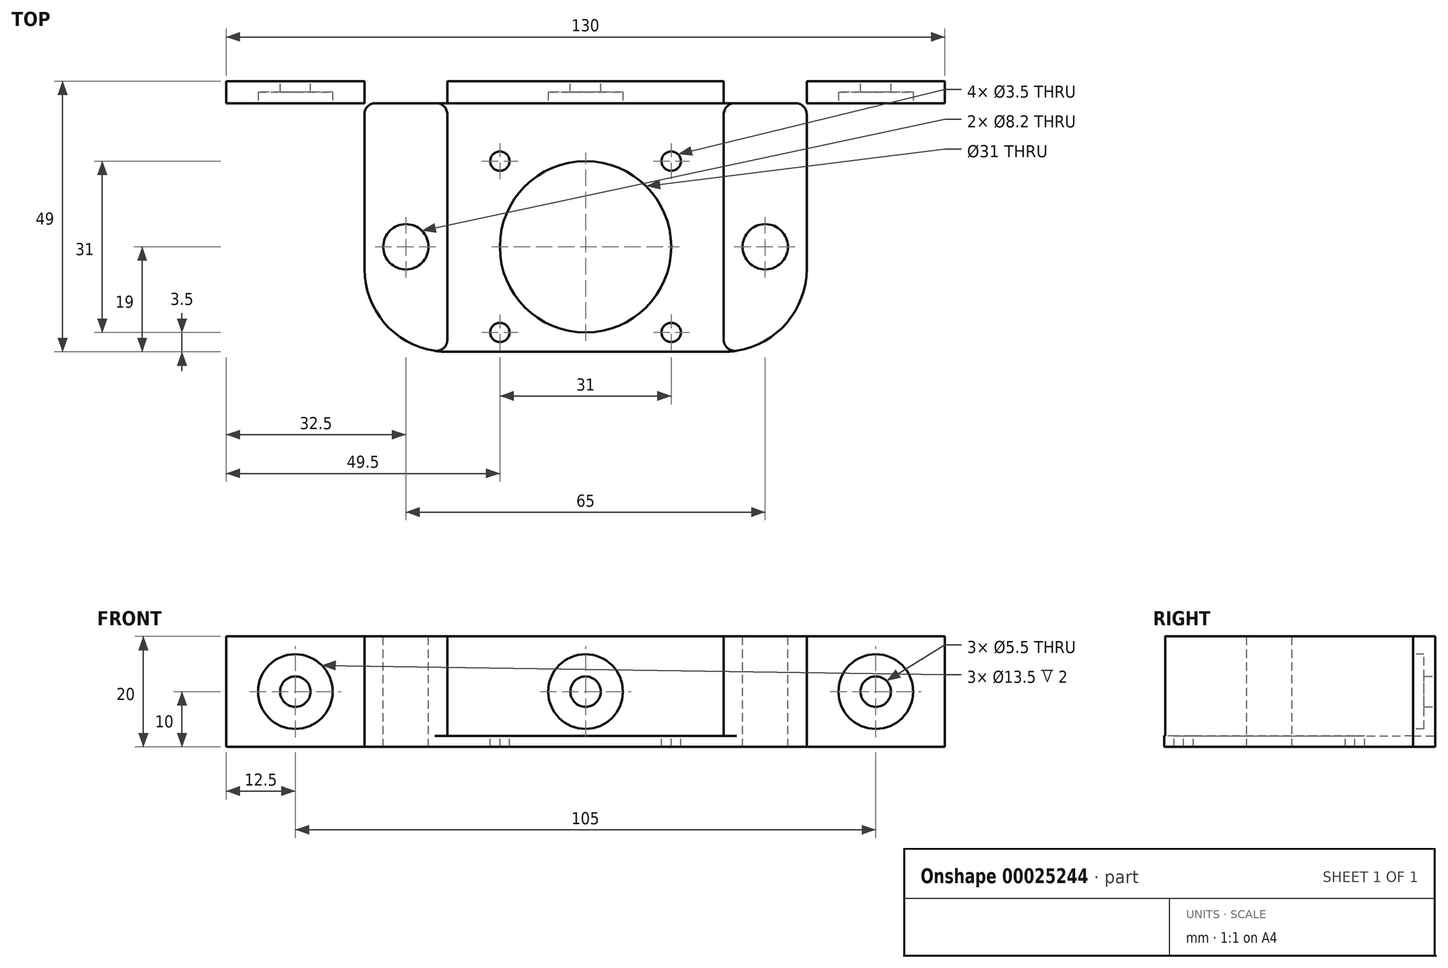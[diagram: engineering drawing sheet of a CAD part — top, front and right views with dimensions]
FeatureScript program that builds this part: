
annotation { "Feature Type Name" : "Feature", "Feature Type Description" : "" }
export const myFeature = defineFeature(function(context is Context, id is Id, definition is map)
    precondition{}
    {
        {
            var Q0;
            Q0=qCreatedBy(makeId("Front.planeOp"),FACE);
            var sketch = newSketch(context, id + "F0", { "sketchPlane" : qUnion([Q0])});
            skLineSegment(sketch, "E0.bottom", {"start": v(0, 0) * mm, "end": v(130, 0) * mm});
            skLineSegment(sketch, "E0.left", {"start": v(0, 0) * mm, "end": v(0, 20) * mm});
            skLineSegment(sketch, "E0.right", {"start": v(130, 0) * mm, "end": v(130, 20) * mm});
            skLineSegment(sketch, "E1.bottom", {"start": v(40, 20) * mm, "end": v(90, 20) * mm});
            skLineSegment(sketch, "E1.top", {"start": v(40, 0) * mm, "end": v(90, 0) * mm});
            skLineSegment(sketch, "E1.left", {"start": v(40, 20) * mm, "end": v(40, 0) * mm});
            skLineSegment(sketch, "E1.right", {"start": v(90, 20) * mm, "end": v(90, 0) * mm});
            skLineSegment(sketch, "E2", {"start": v(0, 20) * mm, "end": v(40, 20) * mm});
            skLineSegment(sketch, "E3", {"start": v(90, 20) * mm, "end": v(130, 20) * mm});
            skLineSegment(sketch, "E4.bottom", {"start": v(40, 20) * mm, "end": v(25, 20) * mm});
            skLineSegment(sketch, "E4.top", {"start": v(40, 0) * mm, "end": v(25, 0) * mm});
            skLineSegment(sketch, "E4.right", {"start": v(25, 20) * mm, "end": v(25, 0) * mm});
            skLineSegment(sketch, "E5.bottom", {"start": v(90, 20) * mm, "end": v(105, 20) * mm});
            skLineSegment(sketch, "E5.top", {"start": v(90, 0) * mm, "end": v(105, 0) * mm});
            skLineSegment(sketch, "E5.right", {"start": v(105, 20) * mm, "end": v(105, 0) * mm});
            skCircle(sketch, "E6", {"center": v(12.5, 10) * mm, "radius": 2.75 * mm});
            skCircle(sketch, "E7", {"center": v(117.5, 10) * mm, "radius": 2.75 * mm});
            skLineSegment(sketch, "E8.top", {"start": v(40, 2) * mm, "end": v(90, 2) * mm});
            skLineSegment(sketch, "E8.left", {"start": v(40, 0) * mm, "end": v(40, 2) * mm});
            skLineSegment(sketch, "E8.right", {"start": v(90, 0) * mm, "end": v(90, 2) * mm});
            skLineSegment(sketch, "E9", {"start": v(0, 10) * mm, "end": v(12.5, 10) * mm});
            skLineSegment(sketch, "E10", {"start": v(12.5, 10) * mm, "end": v(65, 10) * mm});
            skLineSegment(sketch, "E11", {"start": v(117.5, 10) * mm, "end": v(65, 10) * mm});
            skLineSegment(sketch, "E12", {"start": v(117.5, 10) * mm, "end": v(130, 10) * mm});
            skCircle(sketch, "E13", {"center": v(12.5, 10) * mm, "radius": 6.75 * mm});
            skCircle(sketch, "E14", {"center": v(117.5, 10) * mm, "radius": 6.75 * mm});
            skCircle(sketch, "E15", {"center": v(65, 10) * mm, "radius": 2.75 * mm});
            skCircle(sketch, "E16", {"center": v(65.03, 10.1) * mm, "radius": 6.75 * mm});
            skSolve(sketch);
        }
        {
            var Q0;
            {var subQ1=sQuery(id+"F0.wireOp",EDGE,"E0.left");Q0=makeQuery(id+"F0.imprint","IMPRINT",FACE,{"disambiguationData":[TD([[makeQuery(id+"F0.imprint","IMPRINT",EDGE,{"derivedFrom":subQ1}),-1.0]])]});}
            var Q1;
            {var subQ1=sQuery(id+"F0.wireOp",EDGE,"E0.right");Q1=makeQuery(id+"F0.imprint","IMPRINT",FACE,{"disambiguationData":[TD([[makeQuery(id+"F0.imprint","IMPRINT",EDGE,{"derivedFrom":subQ1}),1.0]])]});}
            var Q2;
            Q2=makeQuery(id+"F0.imprint","IMPRINT",FACE,{"disambiguationData":[TD([[makeQuery(id+"F0.imprint","IMPRINT",EDGE,{"derivedFrom":sQuery(id+"F0.wireOp",EDGE,"E1.bottom")}),-1.0]])]});
            var Q3;
            Q3=makeQuery(id+"F0.imprint","IMPRINT",FACE,{"disambiguationData":[TD([[makeQuery(id+"F0.imprint","IMPRINT",EDGE,{"derivedFrom":sQuery(id+"F0.wireOp",EDGE,"E4.bottom")}),1.0]])]});
            var Q4;
            Q4=makeQuery(id+"F0.imprint","IMPRINT",FACE,{"disambiguationData":[TD([[makeQuery(id+"F0.imprint","IMPRINT",EDGE,{"derivedFrom":sQuery(id+"F0.wireOp",EDGE,"E5.bottom")}),-1.0]])]});
            var Q5;
            Q5=makeQuery(id+"F0.imprint","IMPRINT",FACE,{"disambiguationData":[TD([[makeQuery(id+"F0.imprint","IMPRINT",EDGE,{"derivedFrom":sQuery(id+"F0.wireOp",EDGE,"E1.top")}),1.0]])]});
            var Q6;
            {var subQ6=sQuery(id+"F0.wireOp",EDGE,"E4.top");Q6=makeQuery(id+"F0.imprint","IMPRINT",FACE,{"disambiguationData":[TD([[makeQuery(id+"F0.imprint","IMPRINT",EDGE,{"derivedFrom":subQ6}),-1.0]])]});}
            var Q7;
            {var subQ9=sQuery(id+"F0.wireOp",EDGE,"E8.top");Q7=makeQuery(id+"F0.imprint","IMPRINT",FACE,{"disambiguationData":[TD([[makeQuery(id+"F0.imprint","IMPRINT",EDGE,{"derivedFrom":subQ9}),1.0]])]});}
            var Q8;
            {var subQ6=sQuery(id+"F0.wireOp",EDGE,"E5.top");Q8=makeQuery(id+"F0.imprint","IMPRINT",FACE,{"disambiguationData":[TD([[makeQuery(id+"F0.imprint","IMPRINT",EDGE,{"derivedFrom":subQ6}),1.0]])]});}
            var Q9;
            {var subQ3=sQuery(id+"F0.wireOp",EDGE,"E9");var subQ5=sQuery(id+"F0.wireOp",EDGE,"E6");var subQ7=makeQuery(id+"F0.imprint","INTERSECT",VERTEX,{"derivedFrom":[subQ5,subQ3]});Q9=makeQuery(id+"F0.imprint","IMPRINT",FACE,{"disambiguationData":[TD([[makeQuery(id+"F0.imprint","IMPRINT",EDGE,{"disambiguationData":[TD([[subQ7,1.0]])],"derivedFrom":subQ5}),-1.0]])]});}
            var Q10;
            {var subQ3=sQuery(id+"F0.wireOp",EDGE,"E9");var subQ5=sQuery(id+"F0.wireOp",EDGE,"E6");var subQ7=makeQuery(id+"F0.imprint","INTERSECT",VERTEX,{"derivedFrom":[subQ5,subQ3]});Q10=makeQuery(id+"F0.imprint","IMPRINT",FACE,{"disambiguationData":[TD([[makeQuery(id+"F0.imprint","IMPRINT",EDGE,{"disambiguationData":[TD([[subQ7,-1.0]])],"derivedFrom":subQ5}),-1.0]])]});}
            var Q11;
            {var subQ0=sQuery(id+"F0.wireOp",EDGE,"E16");var subQ3=sQuery(id+"F0.wireOp",EDGE,"E10");var subQ4=makeQuery(id+"F0.imprint","INTERSECT",VERTEX,{"derivedFrom":[subQ3,subQ0]});Q11=makeQuery(id+"F0.imprint","IMPRINT",FACE,{"disambiguationData":[TD([[makeQuery(id+"F0.imprint","IMPRINT",EDGE,{"disambiguationData":[TD([[subQ4,-1.0]])],"derivedFrom":subQ3}),-1.0]])]});}
            var Q12;
            {var subQ0=sQuery(id+"F0.wireOp",EDGE,"E16");var subQ3=sQuery(id+"F0.wireOp",EDGE,"E10");var subQ4=makeQuery(id+"F0.imprint","INTERSECT",VERTEX,{"derivedFrom":[subQ3,subQ0]});Q12=makeQuery(id+"F0.imprint","IMPRINT",FACE,{"disambiguationData":[TD([[makeQuery(id+"F0.imprint","IMPRINT",EDGE,{"disambiguationData":[TD([[subQ4,-1.0]])],"derivedFrom":subQ3}),1.0]])]});}
            var Q13;
            {var subQ3=sQuery(id+"F0.wireOp",EDGE,"E11");var subQ5=sQuery(id+"F0.wireOp",EDGE,"E7");var subQ7=makeQuery(id+"F0.imprint","INTERSECT",VERTEX,{"derivedFrom":[subQ5,subQ3]});Q13=makeQuery(id+"F0.imprint","IMPRINT",FACE,{"disambiguationData":[TD([[makeQuery(id+"F0.imprint","IMPRINT",EDGE,{"disambiguationData":[TD([[subQ7,1.0]])],"derivedFrom":subQ5}),-1.0]])]});}
            var Q14;
            {var subQ3=sQuery(id+"F0.wireOp",EDGE,"E11");var subQ5=sQuery(id+"F0.wireOp",EDGE,"E7");var subQ7=makeQuery(id+"F0.imprint","INTERSECT",VERTEX,{"derivedFrom":[subQ5,subQ3]});Q14=makeQuery(id+"F0.imprint","IMPRINT",FACE,{"disambiguationData":[TD([[makeQuery(id+"F0.imprint","IMPRINT",EDGE,{"disambiguationData":[TD([[subQ7,-1.0]])],"derivedFrom":subQ5}),-1.0]])]});}
            extrude(context, id + "F1", {"entities" : qUnion([Q0, Q1, Q2, Q3, Q4, Q5, Q6, Q7, Q8, Q9, Q10, Q11, Q12, Q13, Q14]), "depth" : 4 * mm});
        }
        {
            var Q0;
            Q0=makeQuery(id+"F1.opExtrude","CAP_FACE",FACE,{"disambiguationData":[OSD([sQuery(id+"F0.wireOp",EDGE,"E0.bottom"),sQuery(id+"F0.wireOp",EDGE,"E0.left"),sQuery(id+"F0.wireOp",EDGE,"E0.right"),sQuery(id+"F0.wireOp",EDGE,"E1.bottom"),sQuery(id+"F0.wireOp",EDGE,"E2"),sQuery(id+"F0.wireOp",EDGE,"E3"),sQuery(id+"F0.wireOp",EDGE,"E4.bottom"),sQuery(id+"F0.wireOp",EDGE,"E4.top"),sQuery(id+"F0.wireOp",EDGE,"E5.bottom"),sQuery(id+"F0.wireOp",EDGE,"E5.top"),sQuery(id+"F0.wireOp",EDGE,"E6"),sQuery(id+"F0.wireOp",EDGE,"E7"),sQuery(id+"F0.wireOp",EDGE,"E1.top"),sQuery(id+"F0.wireOp",EDGE,"E15")])],"isStart":false});
            var sketch = newSketch(context, id + "F2", { "sketchPlane" : qUnion([Q0])});
            skCircle(sketch, "E17", {"center": v(12.5, 10) * mm, "radius": 6.75 * mm});
            skCircle(sketch, "E18", {"center": v(65, 10) * mm, "radius": 6.75 * mm});
            skCircle(sketch, "E19", {"center": v(117.5, 10) * mm, "radius": 6.75 * mm});
            skSolve(sketch);
        }
        {
            var Q0;
            Q0 = qSketchRegion(id + "F2", true);
            extrude(context, id + "F3", {"entities" : qUnion([Q0]), "operationType" : NewBodyOperationType.REMOVE, "oppositeDirection" : true, "depth" : 2 * mm});
        }
        {
            var Q0;
            Q0=makeQuery(id+"F1.opExtrude","CAP_FACE",FACE,{"disambiguationData":[OSD([sQuery(id+"F0.wireOp",EDGE,"E0.bottom"),sQuery(id+"F0.wireOp",EDGE,"E0.left"),sQuery(id+"F0.wireOp",EDGE,"E0.right"),sQuery(id+"F0.wireOp",EDGE,"E1.bottom"),sQuery(id+"F0.wireOp",EDGE,"E2"),sQuery(id+"F0.wireOp",EDGE,"E3"),sQuery(id+"F0.wireOp",EDGE,"E4.bottom"),sQuery(id+"F0.wireOp",EDGE,"E4.top"),sQuery(id+"F0.wireOp",EDGE,"E5.bottom"),sQuery(id+"F0.wireOp",EDGE,"E5.top"),sQuery(id+"F0.wireOp",EDGE,"E6"),sQuery(id+"F0.wireOp",EDGE,"E7"),sQuery(id+"F0.wireOp",EDGE,"E1.top")])],"isStart":false});
            var sketch = newSketch(context, id + "F4", { "sketchPlane" : qUnion([Q0])});
            skLineSegment(sketch, "E20.bottom", {"start": v(25, 20) * mm, "end": v(40, 20) * mm});
            skLineSegment(sketch, "E20.top", {"start": v(25, 0) * mm, "end": v(40, 0) * mm});
            skLineSegment(sketch, "E20.left", {"start": v(25, 20) * mm, "end": v(25, 0) * mm});
            skLineSegment(sketch, "E20.right", {"start": v(40, 20) * mm, "end": v(40, 0) * mm});
            skLineSegment(sketch, "E21.bottom", {"start": v(90, 20) * mm, "end": v(105, 20) * mm});
            skLineSegment(sketch, "E21.top", {"start": v(90, 0) * mm, "end": v(105, 0) * mm});
            skLineSegment(sketch, "E21.left", {"start": v(90, 20) * mm, "end": v(90, 0) * mm});
            skLineSegment(sketch, "E21.right", {"start": v(105, 20) * mm, "end": v(105, 0) * mm});
            skLineSegment(sketch, "E22", {"start": v(0, 20) * mm, "end": v(25, 20) * mm});
            skLineSegment(sketch, "E23", {"start": v(105, 20) * mm, "end": v(130, 20) * mm});
            skLineSegment(sketch, "E24.bottom", {"start": v(40, 0) * mm, "end": v(90, 0) * mm});
            skLineSegment(sketch, "E24.top", {"start": v(40, 0) * mm, "end": v(90, 0) * mm});
            skLineSegment(sketch, "E24.left", {"start": v(40, 0) * mm, "end": v(40, 0) * mm});
            skLineSegment(sketch, "E24.right", {"start": v(90, 0) * mm, "end": v(90, 0) * mm});
            skLineSegment(sketch, "E25.bottom", {"start": v(90, 0) * mm, "end": v(40, 0) * mm});
            skLineSegment(sketch, "E25.top", {"start": v(90, 2) * mm, "end": v(40, 2) * mm});
            skLineSegment(sketch, "E25.left", {"start": v(90, 0) * mm, "end": v(90, 2) * mm});
            skLineSegment(sketch, "E25.right", {"start": v(40, 0) * mm, "end": v(40, 2) * mm});
            skSolve(sketch);
        }
        {
            var Q0;
            Q0=qSketchRegion(id+"F4",true);
            extrude(context, id + "F5", {"entities" : qUnion([Q0]), "operationType" : NewBodyOperationType.ADD, "depth" : 45 * mm});
        }
        {
            var Q0;
            Q0=makeQuery(id+"F5.opExtrude","SWEPT_FACE",FACE,{"disambiguationData":[OSD([sQuery(id+"F4.wireOp",EDGE,"E25.top")])]});
            var sketch = newSketch(context, id + "F6", { "sketchPlane" : qUnion([Q0])});
            skLineSegment(sketch, "E26.bottom", {"start": v(43.85, -8.85) * mm, "end": v(86.15, -8.85) * mm});
            skLineSegment(sketch, "E26.top", {"start": v(43.85, -51.15) * mm, "end": v(86.15, -51.15) * mm});
            skLineSegment(sketch, "E26.left", {"start": v(43.85, -8.85) * mm, "end": v(43.85, -51.15) * mm});
            skLineSegment(sketch, "E26.right", {"start": v(86.15, -8.85) * mm, "end": v(86.15, -51.15) * mm});
            skLineSegment(sketch, "E27.bottom", {"start": v(49.5, -14.5) * mm, "end": v(80.5, -14.5) * mm});
            skLineSegment(sketch, "E27.top", {"start": v(49.5, -45.5) * mm, "end": v(80.5, -45.5) * mm});
            skLineSegment(sketch, "E27.left", {"start": v(49.5, -14.5) * mm, "end": v(49.5, -45.5) * mm});
            skLineSegment(sketch, "E27.right", {"start": v(80.5, -14.5) * mm, "end": v(80.5, -45.5) * mm});
            skLineSegment(sketch, "E28", {"start": v(43.85, -51.15) * mm, "end": v(49.5, -45.5) * mm});
            skLineSegment(sketch, "E29", {"start": v(80.5, -14.5) * mm, "end": v(86.15, -8.85) * mm});
            skCircle(sketch, "E30", {"center": v(49.5, -14.5) * mm, "radius": 1.75 * mm});
            skCircle(sketch, "E31", {"center": v(49.5, -45.5) * mm, "radius": 1.75 * mm});
            skCircle(sketch, "E32", {"center": v(80.5, -45.5) * mm, "radius": 1.75 * mm});
            skCircle(sketch, "E33", {"center": v(80.5, -14.5) * mm, "radius": 1.75 * mm});
            skLineSegment(sketch, "E34", {"start": v(65, -30) * mm, "end": v(65, 0) * mm});
            skLineSegment(sketch, "E35", {"start": v(43.85, -51.15) * mm, "end": v(40, -51.15) * mm});
            skLineSegment(sketch, "E36", {"start": v(86.15, -51.15) * mm, "end": v(90, -51.15) * mm});
            skLineSegment(sketch, "E37", {"start": v(49.5, -45.5) * mm, "end": v(65, -30) * mm});
            skLineSegment(sketch, "E38", {"start": v(65, -30) * mm, "end": v(80.5, -14.5) * mm});
            skCircle(sketch, "E39", {"center": v(65, -30) * mm, "radius": 15.5 * mm});
            skSolve(sketch);
        }
        {
            var Q0;
            {var subQ0=sQuery(id+"F6.wireOp",EDGE,"E31");var subQ3=sQuery(id+"F6.wireOp",EDGE,"E27.top");var subQ4=makeQuery(id+"F6.imprint","INTERSECT",VERTEX,{"derivedFrom":[subQ3,subQ0]});Q0=makeQuery(id+"F6.imprint","IMPRINT",FACE,{"disambiguationData":[TD([[makeQuery(id+"F6.imprint","IMPRINT",EDGE,{"disambiguationData":[TD([[subQ4,1.0]])],"derivedFrom":subQ0}),1.0]])]});}
            var Q1;
            {var subQ0=sQuery(id+"F6.wireOp",EDGE,"E31");var subQ3=sQuery(id+"F6.wireOp",EDGE,"E27.left");var subQ4=makeQuery(id+"F6.imprint","INTERSECT",VERTEX,{"derivedFrom":[subQ3,subQ0]});Q1=makeQuery(id+"F6.imprint","IMPRINT",FACE,{"disambiguationData":[TD([[makeQuery(id+"F6.imprint","IMPRINT",EDGE,{"disambiguationData":[TD([[subQ4,-1.0]])],"derivedFrom":subQ0}),1.0]])]});}
            var Q2;
            {var subQ1=sQuery(id+"F6.wireOp",EDGE,"E27.left");var subQ3=sQuery(id+"F6.wireOp",EDGE,"E27.bottom");var subQ5=makeQuery(id+"F6.imprint","INTERSECT",VERTEX,{"derivedFrom":[subQ3,subQ1]});Q2=makeQuery(id+"F6.imprint","IMPRINT",FACE,{"disambiguationData":[TD([[makeQuery(id+"F6.imprint","IMPRINT",EDGE,{"disambiguationData":[TD([[subQ5,-1.0]])],"derivedFrom":subQ3}),-1.0]])]});}
            var Q3;
            {var subQ1=sQuery(id+"F6.wireOp",EDGE,"E27.left");var subQ3=sQuery(id+"F6.wireOp",EDGE,"E27.bottom");var subQ5=makeQuery(id+"F6.imprint","INTERSECT",VERTEX,{"derivedFrom":[subQ3,subQ1]});Q3=makeQuery(id+"F6.imprint","IMPRINT",FACE,{"disambiguationData":[TD([[makeQuery(id+"F6.imprint","IMPRINT",EDGE,{"disambiguationData":[TD([[subQ5,-1.0]])],"derivedFrom":subQ3}),1.0]])]});}
            var Q4;
            {var subQ0=sQuery(id+"F6.wireOp",EDGE,"E33");var subQ3=sQuery(id+"F6.wireOp",EDGE,"E27.bottom");var subQ4=makeQuery(id+"F6.imprint","INTERSECT",VERTEX,{"derivedFrom":[subQ3,subQ0]});Q4=makeQuery(id+"F6.imprint","IMPRINT",FACE,{"disambiguationData":[TD([[makeQuery(id+"F6.imprint","IMPRINT",EDGE,{"disambiguationData":[TD([[subQ4,1.0]])],"derivedFrom":subQ0}),1.0]])]});}
            var Q5;
            {var subQ0=sQuery(id+"F6.wireOp",EDGE,"E33");var subQ3=sQuery(id+"F6.wireOp",EDGE,"E27.bottom");var subQ4=makeQuery(id+"F6.imprint","INTERSECT",VERTEX,{"derivedFrom":[subQ3,subQ0]});Q5=makeQuery(id+"F6.imprint","IMPRINT",FACE,{"disambiguationData":[TD([[makeQuery(id+"F6.imprint","IMPRINT",EDGE,{"disambiguationData":[TD([[subQ4,-1.0]])],"derivedFrom":subQ0}),1.0]])]});}
            var Q6;
            {var subQ0=sQuery(id+"F6.wireOp",EDGE,"E33");var subQ3=sQuery(id+"F6.wireOp",EDGE,"E27.right");var subQ4=makeQuery(id+"F6.imprint","INTERSECT",VERTEX,{"derivedFrom":[subQ3,subQ0]});Q6=makeQuery(id+"F6.imprint","IMPRINT",FACE,{"disambiguationData":[TD([[makeQuery(id+"F6.imprint","IMPRINT",EDGE,{"disambiguationData":[TD([[subQ4,-1.0]])],"derivedFrom":subQ0}),1.0]])]});}
            var Q7;
            {var subQ1=sQuery(id+"F6.wireOp",EDGE,"E27.right");var subQ3=sQuery(id+"F6.wireOp",EDGE,"E27.top");var subQ5=makeQuery(id+"F6.imprint","INTERSECT",VERTEX,{"derivedFrom":[subQ3,subQ1]});Q7=makeQuery(id+"F6.imprint","IMPRINT",FACE,{"disambiguationData":[TD([[makeQuery(id+"F6.imprint","IMPRINT",EDGE,{"disambiguationData":[TD([[subQ5,1.0]])],"derivedFrom":subQ3}),-1.0]])]});}
            var Q8;
            {var subQ1=sQuery(id+"F6.wireOp",EDGE,"E27.right");var subQ3=sQuery(id+"F6.wireOp",EDGE,"E27.top");var subQ5=makeQuery(id+"F6.imprint","INTERSECT",VERTEX,{"derivedFrom":[subQ3,subQ1]});Q8=makeQuery(id+"F6.imprint","IMPRINT",FACE,{"disambiguationData":[TD([[makeQuery(id+"F6.imprint","IMPRINT",EDGE,{"disambiguationData":[TD([[subQ5,1.0]])],"derivedFrom":subQ3}),1.0]])]});}
            var Q9;
            {var subQ1=sQuery(id+"F6.wireOp",EDGE,"E33");var subQ3=sQuery(id+"F6.wireOp",EDGE,"E27.right");var subQ5=makeQuery(id+"F6.imprint","INTERSECT",VERTEX,{"derivedFrom":[subQ3,subQ1]});Q9=makeQuery(id+"F6.imprint","IMPRINT",FACE,{"disambiguationData":[TD([[makeQuery(id+"F6.imprint","IMPRINT",EDGE,{"disambiguationData":[TD([[subQ5,1.0]])],"derivedFrom":subQ1}),1.0]])]});}
            var Q10;
            {var subQ1=sQuery(id+"F6.wireOp",EDGE,"E31");var subQ3=sQuery(id+"F6.wireOp",EDGE,"E27.top");var subQ5=makeQuery(id+"F6.imprint","INTERSECT",VERTEX,{"derivedFrom":[subQ3,subQ1]});Q10=makeQuery(id+"F6.imprint","IMPRINT",FACE,{"disambiguationData":[TD([[makeQuery(id+"F6.imprint","IMPRINT",EDGE,{"disambiguationData":[TD([[subQ5,-1.0]])],"derivedFrom":subQ1}),1.0]])]});}
            var Q11;
            {var subQ1=sQuery(id+"F6.wireOp",EDGE,"E31");var subQ3=sQuery(id+"F6.wireOp",EDGE,"E27.left");var subQ5=makeQuery(id+"F6.imprint","INTERSECT",VERTEX,{"derivedFrom":[subQ3,subQ1]});Q11=makeQuery(id+"F6.imprint","IMPRINT",FACE,{"disambiguationData":[TD([[makeQuery(id+"F6.imprint","IMPRINT",EDGE,{"disambiguationData":[TD([[subQ5,1.0]])],"derivedFrom":subQ1}),1.0]])]});}
            var Q12;
            {var subQ0=sQuery(id+"F6.wireOp",EDGE,"E39");var subQ3=sQuery(id+"F6.wireOp",EDGE,"E34");var subQ4=makeQuery(id+"F6.imprint","INTERSECT",VERTEX,{"derivedFrom":[subQ3,subQ0]});Q12=makeQuery(id+"F6.imprint","IMPRINT",FACE,{"disambiguationData":[TD([[makeQuery(id+"F6.imprint","IMPRINT",EDGE,{"disambiguationData":[TD([[subQ4,-1.0]])],"derivedFrom":subQ0}),1.0]])]});}
            var Q13;
            {var subQ0=sQuery(id+"F6.wireOp",EDGE,"E39");var subQ3=sQuery(id+"F6.wireOp",EDGE,"E34");var subQ4=makeQuery(id+"F6.imprint","INTERSECT",VERTEX,{"derivedFrom":[subQ3,subQ0]});Q13=makeQuery(id+"F6.imprint","IMPRINT",FACE,{"disambiguationData":[TD([[makeQuery(id+"F6.imprint","IMPRINT",EDGE,{"disambiguationData":[TD([[subQ4,1.0]])],"derivedFrom":subQ0}),1.0]])]});}
            var Q14;
            {var subQ0=sQuery(id+"F6.wireOp",EDGE,"E39");var subQ3=sQuery(id+"F6.wireOp",EDGE,"E37");var subQ4=makeQuery(id+"F6.imprint","INTERSECT",VERTEX,{"derivedFrom":[subQ3,subQ0]});Q14=makeQuery(id+"F6.imprint","IMPRINT",FACE,{"disambiguationData":[TD([[makeQuery(id+"F6.imprint","IMPRINT",EDGE,{"disambiguationData":[TD([[subQ4,-1.0]])],"derivedFrom":subQ0}),1.0]])]});}
            extrude(context, id + "F7", {"entities" : qUnion([Q0, Q1, Q2, Q3, Q4, Q5, Q6, Q7, Q8, Q9, Q10, Q11, Q12, Q13, Q14]), "operationType" : NewBodyOperationType.REMOVE, "oppositeDirection" : true, "depth" : 2 * mm});
        }
        {
            var Q0;
            Q0=makeQuery(id+"F5.boolean.opBoolean","MERGE",FACE,{"derivedFrom":[makeQuery(id+"F1.opExtrude","SWEPT_FACE",FACE,{"disambiguationData":[OSD([sQuery(id+"F0.wireOp",EDGE,"E1.bottom"),sQuery(id+"F0.wireOp",EDGE,"E2"),sQuery(id+"F0.wireOp",EDGE,"E3"),sQuery(id+"F0.wireOp",EDGE,"E4.bottom"),sQuery(id+"F0.wireOp",EDGE,"E5.bottom")])]}),makeQuery(id+"F5.opExtrude","SWEPT_FACE",FACE,{"disambiguationData":[OSD([sQuery(id+"F4.wireOp",EDGE,"E20.bottom")])]}),makeQuery(id+"F5.opExtrude","SWEPT_FACE",FACE,{"disambiguationData":[OSD([sQuery(id+"F4.wireOp",EDGE,"E21.bottom")])]})]});
            var sketch = newSketch(context, id + "F8", { "sketchPlane" : qUnion([Q0])});
            skCircle(sketch, "E40", {"center": v(32.5, -30) * mm, "radius": 4.1 * mm});
            skCircle(sketch, "E41", {"center": v(97.5, -30) * mm, "radius": 4.1 * mm});
            skLineSegment(sketch, "E42", {"start": v(32.5, -30) * mm, "end": v(32.5, 0) * mm});
            skLineSegment(sketch, "E43", {"start": v(97.5, -30) * mm, "end": v(97.5, 0) * mm});
            skLineSegment(sketch, "E44", {"start": v(32.5, -30) * mm, "end": v(97.5, -30) * mm});
            skLineSegment(sketch, "E45", {"start": v(32.5, 0) * mm, "end": v(0, 0) * mm});
            skLineSegment(sketch, "E46", {"start": v(97.5, 0) * mm, "end": v(130, 0) * mm});
            skSolve(sketch);
        }
        {
            var Q0;
            {var subQ1=sQuery(id+"F8.wireOp",EDGE,"E40");var subQ3=sQuery(id+"F8.wireOp",EDGE,"E42");var subQ5=makeQuery(id+"F8.imprint","INTERSECT",VERTEX,{"derivedFrom":[subQ1,subQ3]});Q0=makeQuery(id+"F8.imprint","IMPRINT",FACE,{"disambiguationData":[TD([[makeQuery(id+"F8.imprint","IMPRINT",EDGE,{"disambiguationData":[TD([[subQ5,-1.0]])],"derivedFrom":subQ1}),1.0]])]});}
            var Q1;
            {var subQ1=sQuery(id+"F8.wireOp",EDGE,"E40");var subQ3=sQuery(id+"F8.wireOp",EDGE,"E42");var subQ5=makeQuery(id+"F8.imprint","INTERSECT",VERTEX,{"derivedFrom":[subQ1,subQ3]});Q1=makeQuery(id+"F8.imprint","IMPRINT",FACE,{"disambiguationData":[TD([[makeQuery(id+"F8.imprint","IMPRINT",EDGE,{"disambiguationData":[TD([[subQ5,1.0]])],"derivedFrom":subQ1}),1.0]])]});}
            var Q2;
            {var subQ1=sQuery(id+"F8.wireOp",EDGE,"E41");var subQ3=sQuery(id+"F8.wireOp",EDGE,"E43");var subQ5=makeQuery(id+"F8.imprint","INTERSECT",VERTEX,{"derivedFrom":[subQ1,subQ3]});Q2=makeQuery(id+"F8.imprint","IMPRINT",FACE,{"disambiguationData":[TD([[makeQuery(id+"F8.imprint","IMPRINT",EDGE,{"disambiguationData":[TD([[subQ5,-1.0]])],"derivedFrom":subQ1}),1.0]])]});}
            var Q3;
            {var subQ1=sQuery(id+"F8.wireOp",EDGE,"E41");var subQ3=sQuery(id+"F8.wireOp",EDGE,"E43");var subQ5=makeQuery(id+"F8.imprint","INTERSECT",VERTEX,{"derivedFrom":[subQ1,subQ3]});Q3=makeQuery(id+"F8.imprint","IMPRINT",FACE,{"disambiguationData":[TD([[makeQuery(id+"F8.imprint","IMPRINT",EDGE,{"disambiguationData":[TD([[subQ5,1.0]])],"derivedFrom":subQ1}),1.0]])]});}
            extrude(context, id + "F9", {"entities" : qUnion([Q0, Q1, Q2, Q3]), "operationType" : NewBodyOperationType.REMOVE, "oppositeDirection" : true, "depth" : 20 * mm});
        }
        {
            var Q0;
            Q0=makeQuery(id+"F5.opExtrude","CAP_EDGE",EDGE,{"disambiguationData":[OSD([sQuery(id+"F4.wireOp",EDGE,"E20.left")])],"isStart":true});
            var Q1;
            Q1=makeQuery(id+"F5.opExtrude","CAP_EDGE",EDGE,{"disambiguationData":[OSD([sQuery(id+"F4.wireOp",EDGE,"E21.right")])],"isStart":true});
            var Q2;
            Q2=makeQuery(id+"F5.opExtrude","CAP_EDGE",EDGE,{"disambiguationData":[OSD([sQuery(id+"F4.wireOp",EDGE,"E20.right")])],"isStart":true});
            var Q3;
            Q3=makeQuery(id+"F5.opExtrude","CAP_EDGE",EDGE,{"disambiguationData":[OSD([sQuery(id+"F4.wireOp",EDGE,"E21.left")])],"isStart":true});
            fillet(context, id + "F10", {"entities" : qUnion([Q0, Q1, Q2, Q3]), "radius" : 2 * mm, "tangentPropagation" : true, "allowEdgeOverflow" : false});
        }
        {
            var Q0;
            Q0=makeQuery(id+"F5.opExtrude","CAP_EDGE",EDGE,{"disambiguationData":[OSD([sQuery(id+"F4.wireOp",EDGE,"E21.right")])],"isStart":false});
            var Q1;
            Q1=makeQuery(id+"F5.opExtrude","CAP_EDGE",EDGE,{"disambiguationData":[OSD([sQuery(id+"F4.wireOp",EDGE,"E20.left")])],"isStart":false});
            fillet(context, id + "F11", {"entities" : qUnion([Q0, Q1]), "radius" : 15 * mm, "allowEdgeOverflow" : false});
        }
        {
            var Q0;
            Q0=makeQuery(id+"F11.opFillet","BLEND_EDGE",EDGE,{"blendedFrom":[makeQuery(id+"F5.opExtrude","CAP_EDGE",EDGE,{"disambiguationData":[OSD([sQuery(id+"F4.wireOp",EDGE,"E20.left")])],"isStart":false}),makeQuery(id+"F5.opExtrude","SWEPT_FACE",FACE,{"disambiguationData":[OSD([sQuery(id+"F4.wireOp",EDGE,"E20.right")])]})],"blendedInto":[makeQuery(id+"F5.opExtrude","SWEPT_FACE",FACE,{"disambiguationData":[OSD([sQuery(id+"F4.wireOp",EDGE,"E20.right")])]})]});
            var Q1;
            Q1=makeQuery(id+"F11.opFillet","BLEND_EDGE",EDGE,{"blendedFrom":[makeQuery(id+"F5.opExtrude","CAP_EDGE",EDGE,{"disambiguationData":[OSD([sQuery(id+"F4.wireOp",EDGE,"E21.right")])],"isStart":false}),makeQuery(id+"F5.opExtrude","SWEPT_FACE",FACE,{"disambiguationData":[OSD([sQuery(id+"F4.wireOp",EDGE,"E21.left")])]})],"blendedInto":[makeQuery(id+"F5.opExtrude","SWEPT_FACE",FACE,{"disambiguationData":[OSD([sQuery(id+"F4.wireOp",EDGE,"E21.left")])]})]});
            fillet(context, id + "F12", {"entities" : qUnion([Q0, Q1]), "radius" : 2 * mm, "tangentPropagation" : true, "allowEdgeOverflow" : false});
        }
    });
